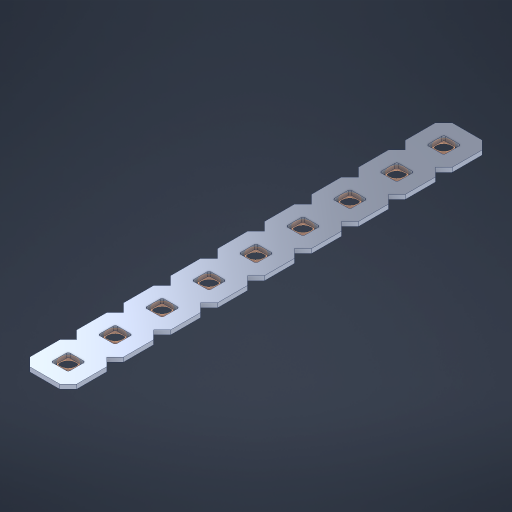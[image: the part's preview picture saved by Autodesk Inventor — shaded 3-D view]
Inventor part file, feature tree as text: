
AUTODESK INVENTOR PART (.ipt)
format: ipt  version: 2023 (Build 270158000, 158)  size: 375,808 bytes
history: native  units: in
note: dims shown in document units (in); Inventor stores cm internally (conversion verified against a paired STEP export)
features: other x10, extrude x8, sketch x2, pattern_linear x1
ambient origin geometry x8: Origin, YZ Plane, XZ Plane, XY Plane, X Axis, Y Axis, Z Axis, Center Point
bodies: Solid1 (feature_tree), Body (feature_tree)
feature tree (21):
  pattern_linear  "Rectangular Pattern1"  Spacing1=0.09in  [1 undecoded]
  sketch  "Sketch1"  dims[d1=0.5in]
  sketch  "Sketch2"  dims[d2=0.182in d3=0.09in d4=0.09in d5=0.09in d6=0.09in d7=0.09in d8=0.09in d9=0.09in d10=0.09in d11=0.02in d13=0.0in d14=0.172in d15=0.0625in d16=0.0in d19=0.5in d22=0.5in]
  other  "Srf1"
  other  "Srf126"
  other  "Srf127"
  other  "Srf128"
  other  "Srf129"
  other  "Srf130"
  other  "Srf131"
  other  "Srf250"
  other  "Srf251"
  other  "Circle"
  extrude  "ExtrusionSrf126"  Depth=0.09in
  extrude  "ExtrusionSrf127"  Depth=0.09in
  extrude  "ExtrusionSrf128"  Depth=0.09in
  extrude  "ExtrusionSrf129"  Depth=0.09in
  extrude  "ExtrusionSrf130"  Depth=0.09in
  extrude  "ExtrusionSrf131"  Depth=0.09in
  extrude  "ExtrusionSrf250"  Depth=0.09in
  extrude  "ExtrusionSrf251"  Depth=0.02in
note: 1 required parameter value undecoded (feature->parameter linkage not recoverable at this tier; creation-order binding heuristic only, values carry confidence <= 0.55)
